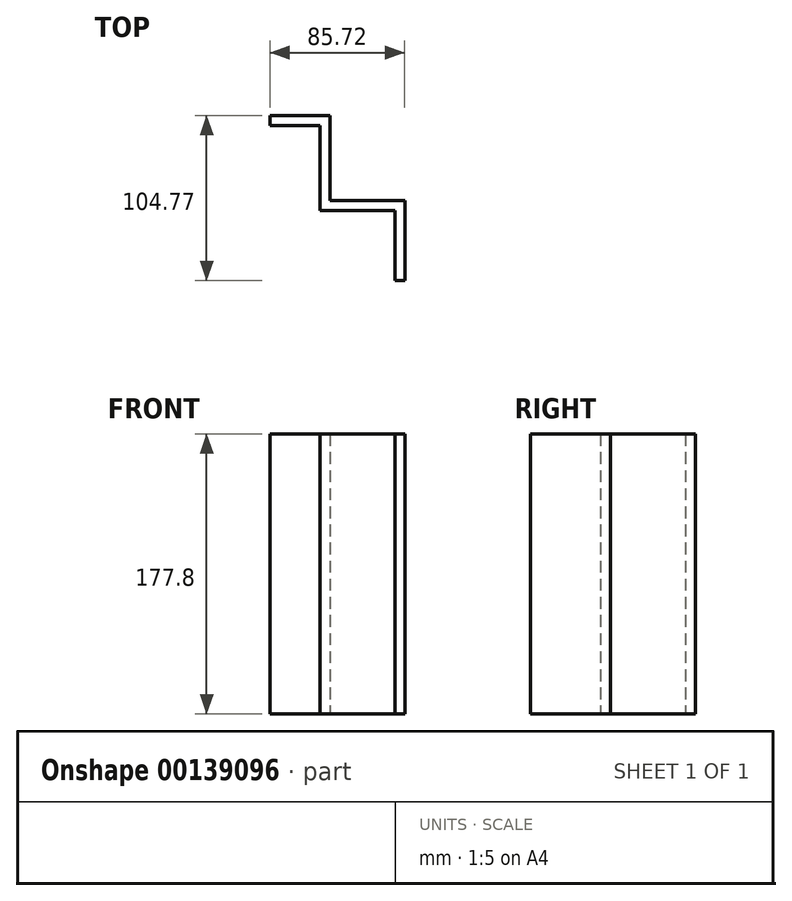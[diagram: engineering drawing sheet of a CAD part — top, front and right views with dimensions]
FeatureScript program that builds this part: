
annotation { "Feature Type Name" : "Feature", "Feature Type Description" : "" }
export const myFeature = defineFeature(function(context is Context, id is Id, definition is map)
    precondition{}
    {
        {
            var Q0;
            Q0=qCreatedBy(makeId("Front.planeOp"),FACE);
            var sketch = newSketch(context, id + "F0", { "sketchPlane" : qUnion([Q0])});
            skLineSegment(sketch, "E0.bottom", {"start": v(0, 0) * mm, "end": v(-38.1, 0) * mm});
            skLineSegment(sketch, "E0.top", {"start": v(0, -177.8) * mm, "end": v(-38.1, -177.8) * mm});
            skLineSegment(sketch, "E0.left", {"start": v(0, 0) * mm, "end": v(0, -177.8) * mm});
            skLineSegment(sketch, "E0.right", {"start": v(-38.1, 0) * mm, "end": v(-38.1, -177.8) * mm});
            skSolve(sketch);
        }
        {
            var Q0;
            Q0 = qSketchRegion(id + "F0", true);
            extrude(context, id + "F1", {"entities" : qUnion([Q0]), "depth" : 6.35 * mm});
        }
        {
            var Q0;
            Q0=makeQuery(id+"F1.opExtrude","CAP_FACE",FACE,{"disambiguationData":[OSD([sQuery(id+"F0.wireOp",EDGE,"E0.bottom"),sQuery(id+"F0.wireOp",EDGE,"E0.top"),sQuery(id+"F0.wireOp",EDGE,"E0.left"),sQuery(id+"F0.wireOp",EDGE,"E0.right")])],"isStart":false});
            var sketch = newSketch(context, id + "F2", { "sketchPlane" : qUnion([Q0])});
            skLineSegment(sketch, "E1.bottom", {"start": v(0, 0) * mm, "end": v(-6.35, 0) * mm});
            skLineSegment(sketch, "E1.top", {"start": v(0, -177.8) * mm, "end": v(-6.35, -177.8) * mm});
            skLineSegment(sketch, "E1.left", {"start": v(0, 0) * mm, "end": v(0, -177.8) * mm});
            skLineSegment(sketch, "E1.right", {"start": v(-6.35, 0) * mm, "end": v(-6.35, -177.8) * mm});
            skSolve(sketch);
        }
        {
            var Q0;
            Q0 = qSketchRegion(id + "F2", true);
            extrude(context, id + "F3", {"entities" : qUnion([Q0]), "operationType" : NewBodyOperationType.ADD, "depth" : 53.97 * mm});
        }
        {
            var Q0;
            Q0=makeQuery(id+"F3.boolean.opBoolean","MERGE",FACE,{"derivedFrom":[makeQuery(id+"F1.opExtrude","SWEPT_FACE",FACE,{"disambiguationData":[OSD([sQuery(id+"F0.wireOp",EDGE,"E0.left")])]}),makeQuery(id+"F3.opExtrude","SWEPT_FACE",FACE,{"disambiguationData":[OSD([sQuery(id+"F2.wireOp",EDGE,"E1.left")])]})]});
            var sketch = newSketch(context, id + "F4", { "sketchPlane" : qUnion([Q0])});
            skLineSegment(sketch, "E2.bottom", {"start": v(-60.33, 0) * mm, "end": v(-53.98, 0) * mm});
            skLineSegment(sketch, "E2.top", {"start": v(-60.33, -177.8) * mm, "end": v(-53.97, -177.8) * mm});
            skLineSegment(sketch, "E2.left", {"start": v(-60.33, 0) * mm, "end": v(-60.33, -177.8) * mm});
            skLineSegment(sketch, "E2.right", {"start": v(-53.98, 0) * mm, "end": v(-53.97, -177.8) * mm});
            skSolve(sketch);
        }
        {
            var Q0;
            Q0 = qSketchRegion(id + "F4", true);
            extrude(context, id + "F5", {"entities" : qUnion([Q0]), "operationType" : NewBodyOperationType.ADD, "depth" : 47.62 * mm});
        }
        {
            var Q0;
            Q0=makeQuery(id+"F5.boolean.opBoolean","MERGE",FACE,{"derivedFrom":[makeQuery(id+"F3.opExtrude","CAP_FACE",FACE,{"disambiguationData":[OSD([sQuery(id+"F2.wireOp",EDGE,"E1.bottom"),sQuery(id+"F2.wireOp",EDGE,"E1.top"),sQuery(id+"F2.wireOp",EDGE,"E1.left"),sQuery(id+"F2.wireOp",EDGE,"E1.right")])],"isStart":false}),makeQuery(id+"F5.opExtrude","SWEPT_FACE",FACE,{"disambiguationData":[OSD([sQuery(id+"F4.wireOp",EDGE,"E2.left")])]})]});
            var sketch = newSketch(context, id + "F6", { "sketchPlane" : qUnion([Q0])});
            skLineSegment(sketch, "E3.bottom", {"start": v(47.63, 0) * mm, "end": v(41.27, 0) * mm});
            skLineSegment(sketch, "E3.top", {"start": v(47.63, -177.8) * mm, "end": v(41.28, -177.8) * mm});
            skLineSegment(sketch, "E3.left", {"start": v(47.63, 0) * mm, "end": v(47.63, -177.8) * mm});
            skLineSegment(sketch, "E3.right", {"start": v(41.27, 0) * mm, "end": v(41.28, -177.8) * mm});
            skSolve(sketch);
        }
        {
            var Q0;
            Q0 = qSketchRegion(id + "F6", true);
            extrude(context, id + "F7", {"entities" : qUnion([Q0]), "operationType" : NewBodyOperationType.ADD, "depth" : 44.45 * mm});
        }
    });
